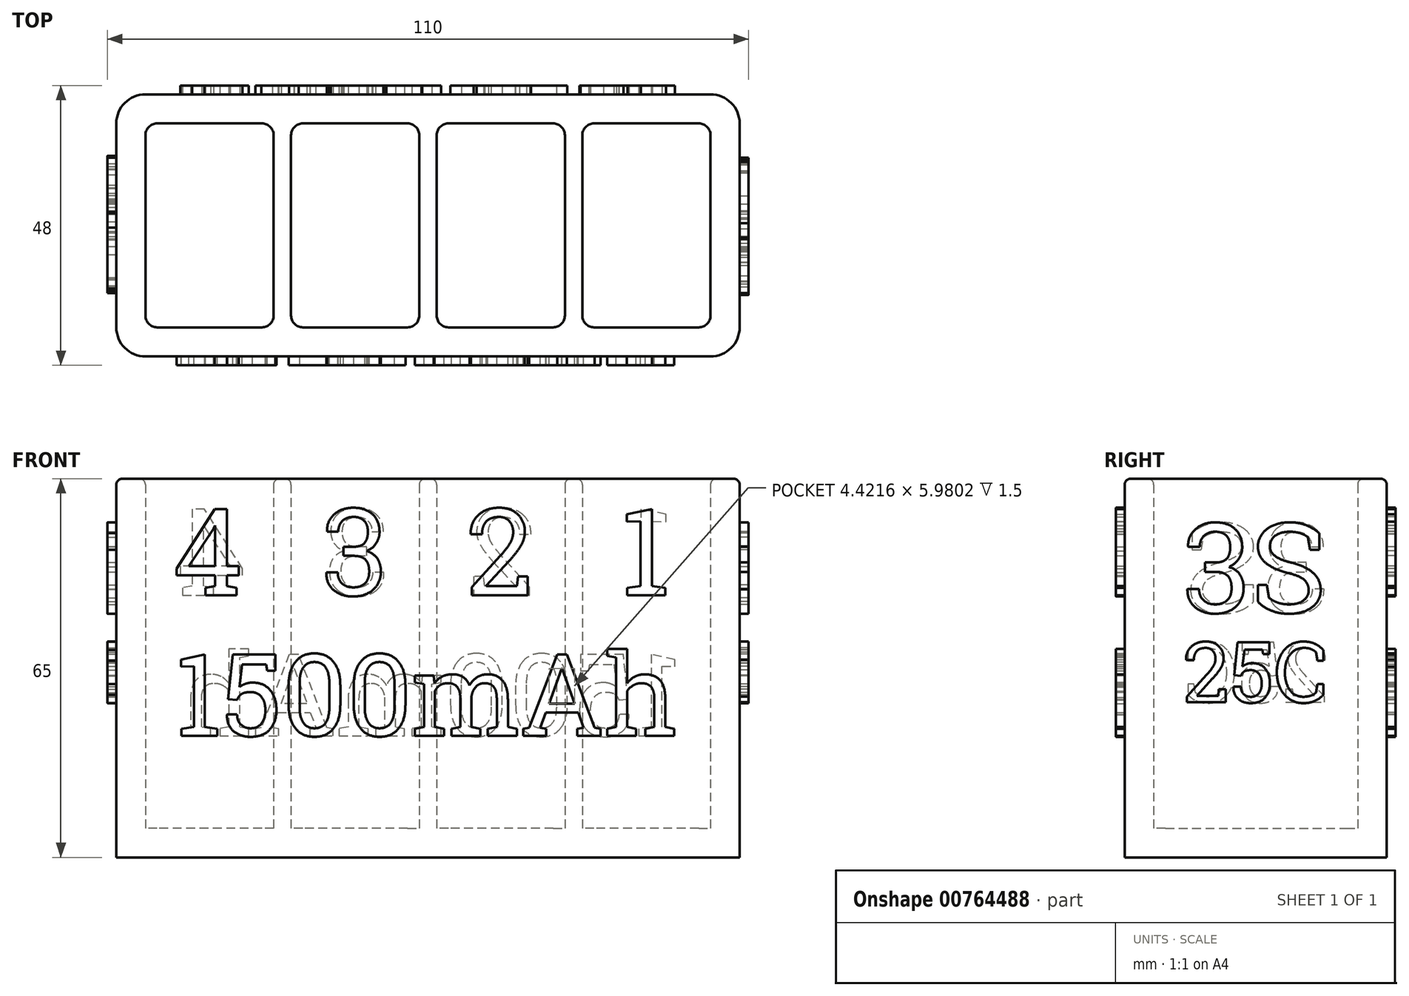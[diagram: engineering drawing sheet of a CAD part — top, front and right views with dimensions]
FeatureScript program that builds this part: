
annotation { "Feature Type Name" : "Feature", "Feature Type Description" : "" }
export const myFeature = defineFeature(function(context is Context, id is Id, definition is map)
    precondition{}
    {
        {
            var Q0;
            Q0=qCreatedBy(makeId("Top.planeOp"),FACE);
            var sketch = newSketch(context, id + "F0", { "sketchPlane" : qUnion([Q0])});
            skLineSegment(sketch, "E0.bottom", {"start": v(53.5, -22.5) * mm, "end": v(-53.5, -22.5) * mm});
            skLineSegment(sketch, "E0.top", {"start": v(53.5, 22.5) * mm, "end": v(-53.5, 22.5) * mm});
            skLineSegment(sketch, "E0.left", {"start": v(53.5, -22.5) * mm, "end": v(53.5, 22.5) * mm});
            skLineSegment(sketch, "E0.right", {"start": v(-53.5, -22.5) * mm, "end": v(-53.5, 22.5) * mm});
            skPoint(sketch, "E0.middle", {"position": v(0, 0) * mm});
            skLineSegment(sketch, "E1.bottom", {"start": v(-26.5, -17.5) * mm, "end": v(-48.5, -17.5) * mm});
            skLineSegment(sketch, "E1.top", {"start": v(-26.5, 17.5) * mm, "end": v(-48.5, 17.5) * mm});
            skLineSegment(sketch, "E1.left", {"start": v(-26.5, -17.5) * mm, "end": v(-26.5, 17.5) * mm});
            skLineSegment(sketch, "E1.right", {"start": v(-48.5, -17.5) * mm, "end": v(-48.5, 17.5) * mm});
            skPoint(sketch, "E1.middle", {"position": v(-37.5, 0) * mm});
            skLineSegment(sketch, "E2.1.0.0", {"start": v(-1.5, 17.5) * mm, "end": v(-23.5, 17.5) * mm});
            skLineSegment(sketch, "E2.1.0.1", {"start": v(-23.5, -17.5) * mm, "end": v(-23.5, 17.5) * mm});
            skLineSegment(sketch, "E2.1.0.2", {"start": v(-1.5, -17.5) * mm, "end": v(-23.5, -17.5) * mm});
            skLineSegment(sketch, "E2.1.0.3", {"start": v(-1.5, -17.5) * mm, "end": v(-1.5, 17.5) * mm});
            skLineSegment(sketch, "E2.2.0.0", {"start": v(23.5, 17.5) * mm, "end": v(1.5, 17.5) * mm});
            skLineSegment(sketch, "E2.2.0.1", {"start": v(1.5, -17.5) * mm, "end": v(1.5, 17.5) * mm});
            skLineSegment(sketch, "E2.2.0.2", {"start": v(23.5, -17.5) * mm, "end": v(1.5, -17.5) * mm});
            skLineSegment(sketch, "E2.2.0.3", {"start": v(23.5, -17.5) * mm, "end": v(23.5, 17.5) * mm});
            skLineSegment(sketch, "E2.3.0.0", {"start": v(48.5, 17.5) * mm, "end": v(26.5, 17.5) * mm});
            skLineSegment(sketch, "E2.3.0.1", {"start": v(26.5, -17.5) * mm, "end": v(26.5, 17.5) * mm});
            skLineSegment(sketch, "E2.3.0.2", {"start": v(48.5, -17.5) * mm, "end": v(26.5, -17.5) * mm});
            skLineSegment(sketch, "E2.3.0.3", {"start": v(48.5, -17.5) * mm, "end": v(48.5, 17.5) * mm});
            skLineSegment(sketch, "E2.direction1", {"start": v(-48.5, 17.5) * mm, "end": v(-23.5, 17.5) * mm, "construction": true});
            skSolve(sketch);
        }
        {
            var Q0;
            Q0=makeQuery(id+"F0.imprint","IMPRINT",FACE,{"disambiguationData":[TD([[makeQuery(id+"F0.imprint","IMPRINT",EDGE,{"derivedFrom":sQuery(id+"F0.wireOp",EDGE,"E0.bottom")}),-1.0]])]});
            var Q1;
            Q1=makeQuery(id+"F0.imprint","IMPRINT",FACE,{"disambiguationData":[TD([[makeQuery(id+"F0.imprint","IMPRINT",EDGE,{"derivedFrom":sQuery(id+"F0.wireOp",EDGE,"E2.2.0.0")}),1.0]])]});
            var Q2;
            Q2=makeQuery(id+"F0.imprint","IMPRINT",FACE,{"disambiguationData":[TD([[makeQuery(id+"F0.imprint","IMPRINT",EDGE,{"derivedFrom":sQuery(id+"F0.wireOp",EDGE,"E2.3.0.0")}),1.0]])]});
            var Q3;
            Q3=makeQuery(id+"F0.imprint","IMPRINT",FACE,{"disambiguationData":[TD([[makeQuery(id+"F0.imprint","IMPRINT",EDGE,{"derivedFrom":sQuery(id+"F0.wireOp",EDGE,"E2.1.0.0")}),1.0]])]});
            var Q4;
            Q4=makeQuery(id+"F0.imprint","IMPRINT",FACE,{"disambiguationData":[TD([[makeQuery(id+"F0.imprint","IMPRINT",EDGE,{"derivedFrom":sQuery(id+"F0.wireOp",EDGE,"E1.bottom")}),-1.0]])]});
            extrude(context, id + "F1", {"entities" : qUnion([Q0, Q1, Q2, Q3, Q4]), "oppositeDirection" : true, "depth" : 5 * mm, "offsetDistance" : 25 * mm});
        }
        {
            var Q0;
            Q0=makeQuery(id+"F0.imprint","IMPRINT",FACE,{"disambiguationData":[TD([[makeQuery(id+"F0.imprint","IMPRINT",EDGE,{"derivedFrom":sQuery(id+"F0.wireOp",EDGE,"E0.bottom")}),-1.0]])]});
            extrude(context, id + "F2", {"entities" : qUnion([Q0]), "operationType" : NewBodyOperationType.ADD, "depth" : 60 * mm, "offsetDistance" : 25 * mm});
        }
        {
            var Q0;
            Q0=makeQuery(id+"F2.opExtrude","SWEPT_EDGE",EDGE,{"disambiguationData":[OSD([sQuery(id+"F0.wireOp",EDGE,"E1.top"),sQuery(id+"F0.wireOp",EDGE,"E1.right")])]});
            var Q1;
            Q1=makeQuery(id+"F2.opExtrude","SWEPT_EDGE",EDGE,{"disambiguationData":[OSD([sQuery(id+"F0.wireOp",EDGE,"E1.bottom"),sQuery(id+"F0.wireOp",EDGE,"E1.right")])]});
            var Q2;
            Q2=makeQuery(id+"F2.opExtrude","SWEPT_EDGE",EDGE,{"disambiguationData":[OSD([sQuery(id+"F0.wireOp",EDGE,"E1.bottom"),sQuery(id+"F0.wireOp",EDGE,"E1.left")])]});
            var Q3;
            Q3=makeQuery(id+"F2.opExtrude","SWEPT_EDGE",EDGE,{"disambiguationData":[OSD([sQuery(id+"F0.wireOp",EDGE,"E1.top"),sQuery(id+"F0.wireOp",EDGE,"E1.left")])]});
            var Q4;
            Q4=makeQuery(id+"F2.opExtrude","SWEPT_EDGE",EDGE,{"disambiguationData":[OSD([sQuery(id+"F0.wireOp",EDGE,"E2.1.0.0"),sQuery(id+"F0.wireOp",EDGE,"E2.1.0.3")])]});
            var Q5;
            Q5=makeQuery(id+"F2.opExtrude","SWEPT_EDGE",EDGE,{"disambiguationData":[OSD([sQuery(id+"F0.wireOp",EDGE,"E2.2.0.0"),sQuery(id+"F0.wireOp",EDGE,"E2.2.0.3")])]});
            var Q6;
            Q6=makeQuery(id+"F2.opExtrude","SWEPT_EDGE",EDGE,{"disambiguationData":[OSD([sQuery(id+"F0.wireOp",EDGE,"E2.3.0.0"),sQuery(id+"F0.wireOp",EDGE,"E2.3.0.3")])]});
            var Q7;
            Q7=makeQuery(id+"F2.opExtrude","SWEPT_EDGE",EDGE,{"disambiguationData":[OSD([sQuery(id+"F0.wireOp",EDGE,"E2.1.0.2"),sQuery(id+"F0.wireOp",EDGE,"E2.1.0.3")])]});
            var Q8;
            Q8=makeQuery(id+"F2.opExtrude","SWEPT_EDGE",EDGE,{"disambiguationData":[OSD([sQuery(id+"F0.wireOp",EDGE,"E2.2.0.2"),sQuery(id+"F0.wireOp",EDGE,"E2.2.0.3")])]});
            var Q9;
            Q9=makeQuery(id+"F2.opExtrude","SWEPT_EDGE",EDGE,{"disambiguationData":[OSD([sQuery(id+"F0.wireOp",EDGE,"E2.3.0.2"),sQuery(id+"F0.wireOp",EDGE,"E2.3.0.3")])]});
            var Q10;
            Q10=makeQuery(id+"F2.opExtrude","SWEPT_EDGE",EDGE,{"disambiguationData":[OSD([sQuery(id+"F0.wireOp",EDGE,"E2.3.0.1"),sQuery(id+"F0.wireOp",EDGE,"E2.3.0.2")])]});
            var Q11;
            Q11=makeQuery(id+"F2.opExtrude","SWEPT_EDGE",EDGE,{"disambiguationData":[OSD([sQuery(id+"F0.wireOp",EDGE,"E2.2.0.1"),sQuery(id+"F0.wireOp",EDGE,"E2.2.0.2")])]});
            var Q12;
            Q12=makeQuery(id+"F2.opExtrude","SWEPT_EDGE",EDGE,{"disambiguationData":[OSD([sQuery(id+"F0.wireOp",EDGE,"E2.1.0.1"),sQuery(id+"F0.wireOp",EDGE,"E2.1.0.2")])]});
            var Q13;
            Q13=makeQuery(id+"F2.opExtrude","SWEPT_EDGE",EDGE,{"disambiguationData":[OSD([sQuery(id+"F0.wireOp",EDGE,"E2.1.0.0"),sQuery(id+"F0.wireOp",EDGE,"E2.1.0.1")])]});
            var Q14;
            Q14=makeQuery(id+"F2.opExtrude","SWEPT_EDGE",EDGE,{"disambiguationData":[OSD([sQuery(id+"F0.wireOp",EDGE,"E2.2.0.0"),sQuery(id+"F0.wireOp",EDGE,"E2.2.0.1")])]});
            var Q15;
            Q15=makeQuery(id+"F2.opExtrude","SWEPT_EDGE",EDGE,{"disambiguationData":[OSD([sQuery(id+"F0.wireOp",EDGE,"E2.3.0.0"),sQuery(id+"F0.wireOp",EDGE,"E2.3.0.1")])]});
            fillet(context, id + "F3", {"entities" : qUnion([Q0, Q1, Q2, Q3, Q4, Q5, Q6, Q7, Q8, Q9, Q10, Q11, Q12, Q13, Q14, Q15]), "radius" : 2 * mm, "tangentPropagation" : true, "allowEdgeOverflow" : false});
        }
        {
            var Q0;
            {var subQ0=sQuery(id+"F0.wireOp",EDGE,"E0.right");var subQ1=sQuery(id+"F0.wireOp",EDGE,"E0.bottom");Q0=makeQuery(id+"F2.boolean.opBoolean","MERGE",EDGE,{"derivedFrom":[makeQuery(id+"F1.opExtrude","SWEPT_EDGE",EDGE,{"disambiguationData":[OSD([subQ1,subQ0])]}),makeQuery(id+"F2.opExtrude","SWEPT_EDGE",EDGE,{"disambiguationData":[OSD([subQ1,subQ0])]})]});}
            var Q1;
            {var subQ0=sQuery(id+"F0.wireOp",EDGE,"E0.left");var subQ1=sQuery(id+"F0.wireOp",EDGE,"E0.bottom");Q1=makeQuery(id+"F2.boolean.opBoolean","MERGE",EDGE,{"derivedFrom":[makeQuery(id+"F1.opExtrude","SWEPT_EDGE",EDGE,{"disambiguationData":[OSD([subQ1,subQ0])]}),makeQuery(id+"F2.opExtrude","SWEPT_EDGE",EDGE,{"disambiguationData":[OSD([subQ1,subQ0])]})]});}
            var Q2;
            {var subQ0=sQuery(id+"F0.wireOp",EDGE,"E0.left");var subQ1=sQuery(id+"F0.wireOp",EDGE,"E0.top");Q2=makeQuery(id+"F2.boolean.opBoolean","MERGE",EDGE,{"derivedFrom":[makeQuery(id+"F1.opExtrude","SWEPT_EDGE",EDGE,{"disambiguationData":[OSD([subQ1,subQ0])]}),makeQuery(id+"F2.opExtrude","SWEPT_EDGE",EDGE,{"disambiguationData":[OSD([subQ1,subQ0])]})]});}
            var Q3;
            {var subQ0=sQuery(id+"F0.wireOp",EDGE,"E0.right");var subQ1=sQuery(id+"F0.wireOp",EDGE,"E0.top");Q3=makeQuery(id+"F2.boolean.opBoolean","MERGE",EDGE,{"derivedFrom":[makeQuery(id+"F1.opExtrude","SWEPT_EDGE",EDGE,{"disambiguationData":[OSD([subQ1,subQ0])]}),makeQuery(id+"F2.opExtrude","SWEPT_EDGE",EDGE,{"disambiguationData":[OSD([subQ1,subQ0])]})]});}
            fillet(context, id + "F4", {"entities" : qUnion([Q0, Q1, Q2, Q3]), "radius" : 5 * mm, "tangentPropagation" : true, "allowEdgeOverflow" : false});
        }
        {
            var Q0;
            Q0=makeQuery(id+"F2.opExtrude","CAP_EDGE",EDGE,{"disambiguationData":[OSD([sQuery(id+"F0.wireOp",EDGE,"E1.top")])],"isStart":false});
            var Q1;
            {var subQ0=sQuery(id+"F0.wireOp",EDGE,"E1.right");var subQ1=sQuery(id+"F0.wireOp",EDGE,"E1.top");Q1=makeQuery(id+"F3.opFillet","BLEND_EDGE",EDGE,{"blendedFrom":[makeQuery(id+"F2.opExtrude","SWEPT_EDGE",EDGE,{"disambiguationData":[OSD([subQ1,subQ0])]}),makeQuery(id+"F2.opExtrude","CAP_FACE",FACE,{"disambiguationData":[OSD([sQuery(id+"F0.wireOp",EDGE,"E0.bottom"),sQuery(id+"F0.wireOp",EDGE,"E0.top"),sQuery(id+"F0.wireOp",EDGE,"E0.left"),sQuery(id+"F0.wireOp",EDGE,"E0.right"),sQuery(id+"F0.wireOp",EDGE,"E1.bottom"),subQ1,sQuery(id+"F0.wireOp",EDGE,"E1.left"),subQ0,sQuery(id+"F0.wireOp",EDGE,"E2.1.0.0"),sQuery(id+"F0.wireOp",EDGE,"E2.1.0.1"),sQuery(id+"F0.wireOp",EDGE,"E2.1.0.2"),sQuery(id+"F0.wireOp",EDGE,"E2.1.0.3"),sQuery(id+"F0.wireOp",EDGE,"E2.2.0.0"),sQuery(id+"F0.wireOp",EDGE,"E2.2.0.1"),sQuery(id+"F0.wireOp",EDGE,"E2.2.0.2"),sQuery(id+"F0.wireOp",EDGE,"E2.2.0.3"),sQuery(id+"F0.wireOp",EDGE,"E2.3.0.0"),sQuery(id+"F0.wireOp",EDGE,"E2.3.0.1"),sQuery(id+"F0.wireOp",EDGE,"E2.3.0.2"),sQuery(id+"F0.wireOp",EDGE,"E2.3.0.3")])],"isStart":false})],"blendedInto":[makeQuery(id+"F2.opExtrude","CAP_FACE",FACE,{"disambiguationData":[OSD([sQuery(id+"F0.wireOp",EDGE,"E0.bottom"),sQuery(id+"F0.wireOp",EDGE,"E0.top"),sQuery(id+"F0.wireOp",EDGE,"E0.left"),sQuery(id+"F0.wireOp",EDGE,"E0.right"),sQuery(id+"F0.wireOp",EDGE,"E1.bottom"),subQ1,sQuery(id+"F0.wireOp",EDGE,"E1.left"),subQ0,sQuery(id+"F0.wireOp",EDGE,"E2.1.0.0"),sQuery(id+"F0.wireOp",EDGE,"E2.1.0.1"),sQuery(id+"F0.wireOp",EDGE,"E2.1.0.2"),sQuery(id+"F0.wireOp",EDGE,"E2.1.0.3"),sQuery(id+"F0.wireOp",EDGE,"E2.2.0.0"),sQuery(id+"F0.wireOp",EDGE,"E2.2.0.1"),sQuery(id+"F0.wireOp",EDGE,"E2.2.0.2"),sQuery(id+"F0.wireOp",EDGE,"E2.2.0.3"),sQuery(id+"F0.wireOp",EDGE,"E2.3.0.0"),sQuery(id+"F0.wireOp",EDGE,"E2.3.0.1"),sQuery(id+"F0.wireOp",EDGE,"E2.3.0.2"),sQuery(id+"F0.wireOp",EDGE,"E2.3.0.3")])],"isStart":false})]});}
            var Q2;
            {var subQ0=sQuery(id+"F0.wireOp",EDGE,"E1.right");Q2=makeQuery(id+"F3.opFillet","BLEND_EDGE",EDGE,{"blendedFrom":[makeQuery(id+"F2.opExtrude","SWEPT_EDGE",EDGE,{"disambiguationData":[OSD([sQuery(id+"F0.wireOp",EDGE,"E1.top"),subQ0])]}),makeQuery(id+"F2.opExtrude","SWEPT_FACE",FACE,{"disambiguationData":[OSD([subQ0])]})],"blendedInto":[makeQuery(id+"F2.opExtrude","SWEPT_FACE",FACE,{"disambiguationData":[OSD([subQ0])]})]});}
            var Q3;
            Q3=makeQuery(id+"F2.opExtrude","CAP_EDGE",EDGE,{"disambiguationData":[OSD([sQuery(id+"F0.wireOp",EDGE,"E2.1.0.0")])],"isStart":false});
            var Q4;
            Q4=makeQuery(id+"F2.opExtrude","CAP_EDGE",EDGE,{"disambiguationData":[OSD([sQuery(id+"F0.wireOp",EDGE,"E2.2.0.0")])],"isStart":false});
            var Q5;
            Q5=makeQuery(id+"F2.opExtrude","CAP_EDGE",EDGE,{"disambiguationData":[OSD([sQuery(id+"F0.wireOp",EDGE,"E2.3.0.0")])],"isStart":false});
            fillet(context, id + "F5", {"entities" : qUnion([Q0, Q1, Q2, Q3, Q4, Q5]), "radius" : 1 * mm, "tangentPropagation" : true, "allowEdgeOverflow" : false});
        }
        {
            var Q0;
            Q0=makeQuery(id+"F2.opExtrude","CAP_FACE",FACE,{"disambiguationData":[OSD([sQuery(id+"F0.wireOp",EDGE,"E0.bottom"),sQuery(id+"F0.wireOp",EDGE,"E0.top"),sQuery(id+"F0.wireOp",EDGE,"E0.left"),sQuery(id+"F0.wireOp",EDGE,"E0.right"),sQuery(id+"F0.wireOp",EDGE,"E1.bottom"),sQuery(id+"F0.wireOp",EDGE,"E1.top"),sQuery(id+"F0.wireOp",EDGE,"E1.left"),sQuery(id+"F0.wireOp",EDGE,"E1.right"),sQuery(id+"F0.wireOp",EDGE,"E2.1.0.0"),sQuery(id+"F0.wireOp",EDGE,"E2.1.0.1"),sQuery(id+"F0.wireOp",EDGE,"E2.1.0.2"),sQuery(id+"F0.wireOp",EDGE,"E2.1.0.3"),sQuery(id+"F0.wireOp",EDGE,"E2.2.0.0"),sQuery(id+"F0.wireOp",EDGE,"E2.2.0.1"),sQuery(id+"F0.wireOp",EDGE,"E2.2.0.2"),sQuery(id+"F0.wireOp",EDGE,"E2.2.0.3"),sQuery(id+"F0.wireOp",EDGE,"E2.3.0.0"),sQuery(id+"F0.wireOp",EDGE,"E2.3.0.1"),sQuery(id+"F0.wireOp",EDGE,"E2.3.0.2"),sQuery(id+"F0.wireOp",EDGE,"E2.3.0.3")])],"isStart":false});
            var sketch = newSketch(context, id + "F6", { "sketchPlane" : qUnion([Q0])});
            skPoint(sketch, "E3", {"position": v(37.5, 22.5) * mm});
            skPoint(sketch, "E3.positionSnap0", {"position": v(37.5, 18.5) * mm});
            skPoint(sketch, "E4", {"position": v(12.5, 22.5) * mm});
            skPoint(sketch, "E4.positionSnap0", {"position": v(12.5, 18.5) * mm});
            skPoint(sketch, "E5", {"position": v(-12.5, 22.5) * mm});
            skPoint(sketch, "E5.positionSnap0", {"position": v(-12.5, 18.5) * mm});
            skPoint(sketch, "E6", {"position": v(-37.5, 22.5) * mm});
            skPoint(sketch, "E6.positionSnap0", {"position": v(-37.5, 18.5) * mm});
            skPoint(sketch, "E7", {"position": v(-37.5, -22.5) * mm});
            skPoint(sketch, "E7.positionSnap0", {"position": v(-37.5, -18.5) * mm});
            skPoint(sketch, "E8", {"position": v(-12.5, -22.5) * mm});
            skPoint(sketch, "E9", {"position": v(-12.5, -18.5) * mm});
            skPoint(sketch, "E10", {"position": v(12.5, -18.5) * mm});
            skPoint(sketch, "E11", {"position": v(12.5, -22.5) * mm});
            skPoint(sketch, "E12", {"position": v(37.5, -18.5) * mm});
            skPoint(sketch, "E13", {"position": v(37.5, -22.5) * mm});
            skSolve(sketch);
        }
        {
            var Q0;
            {var subQ0=sQuery(id+"F0.wireOp",EDGE,"E0.top");Q0=makeQuery(id+"F2.boolean.opBoolean","MERGE",FACE,{"derivedFrom":[makeQuery(id+"F1.opExtrude","SWEPT_FACE",FACE,{"disambiguationData":[OSD([subQ0])]}),makeQuery(id+"F2.opExtrude","SWEPT_FACE",FACE,{"disambiguationData":[OSD([subQ0])]})]});}
            var sketch = newSketch(context, id + "F7", { "sketchPlane" : qUnion([Q0])});
            skText(sketch, "E14", { "text": "1", "fontName": "RobotoSlab-Regular.ttf"});
            skText(sketch, "E15", { "text": "2", "fontName": "RobotoSlab-Regular.ttf"});
            skText(sketch, "E16", { "text": "3", "fontName": "RobotoSlab-Regular.ttf"});
            skText(sketch, "E17", { "text": "4", "fontName": "RobotoSlab-Regular.ttf"});
            skLineSegment(sketch, "E18", {"start": v(-54.85, 55) * mm, "end": v(56.37, 55) * mm, "construction": true});
            skLineSegment(sketch, "E19", {"start": v(-37.5, 60) * mm, "end": v(-37.5, 29.3) * mm, "construction": true});
            skLineSegment(sketch, "E20", {"start": v(-12.5, 60) * mm, "end": v(-12.5, 29.73) * mm, "construction": true});
            skLineSegment(sketch, "E21", {"start": v(12.5, 60) * mm, "end": v(12.5, 29) * mm, "construction": true});
            skLineSegment(sketch, "E22", {"start": v(37.5, 60) * mm, "end": v(37.5, 28.2) * mm, "construction": true});
            skLineSegment(sketch, "E23", {"start": v(-56.25, 40) * mm, "end": v(59.34, 40) * mm, "construction": true});
            skText(sketch, "E24", { "text": "1500mAh", "fontName": "RobotoSlab-Regular.ttf"});
            const initialGuessF7  = {"E14": [-0.04205, 0.04, 1, 0, 0.015], "E15": [-0.01844, 0.04, 1, 0, 0.015], "E16": [0.0068, 0.04, 1, 0, 0.015], "E17": [0.03119, 0.04, 1, 0, 0.015], "E24": [-0.0435, 0.01589, 1, 0, 0.01411]};
            skSetInitialGuess(sketch, initialGuessF7);
            skSolve(sketch);
        }
        {
            var Q0;
            {var subQ0=sQuery(id+"F0.wireOp",EDGE,"E0.bottom");Q0=makeQuery(id+"F2.boolean.opBoolean","MERGE",FACE,{"derivedFrom":[makeQuery(id+"F1.opExtrude","SWEPT_FACE",FACE,{"disambiguationData":[OSD([subQ0])]}),makeQuery(id+"F2.opExtrude","SWEPT_FACE",FACE,{"disambiguationData":[OSD([subQ0])]})]});}
            var sketch = newSketch(context, id + "F8", { "sketchPlane" : qUnion([Q0])});
            skLineSegment(sketch, "E25", {"start": v(-59.89, 55) * mm, "end": v(65.59, 55) * mm, "construction": true});
            skLineSegment(sketch, "E26", {"start": v(-59.89, 40) * mm, "end": v(64.96, 40) * mm, "construction": true});
            skText(sketch, "E27", { "text": "1", "fontName": "RobotoSlab-Regular.ttf"});
            skText(sketch, "E28", { "text": "2", "fontName": "RobotoSlab-Regular.ttf"});
            skText(sketch, "E29", { "text": "3", "fontName": "RobotoSlab-Regular.ttf"});
            skText(sketch, "E30", { "text": "4", "fontName": "RobotoSlab-Regular.ttf"});
            skText(sketch, "E31", { "text": "1500mAh", "fontName": "RobotoSlab-Regular.ttf"});
            const initialGuessF8  = {"E27": [0.03295, 0.04, 1, 0, 0.015], "E28": [0.00656, 0.04, 1, 0, 0.015], "E29": [-0.0182, 0.04, 1, 0, 0.015], "E30": [-0.04381, 0.04, 1, 0, 0.015], "E31": [-0.0435, 0.01589, 1, 0, 0.01411]};
            skSetInitialGuess(sketch, initialGuessF8);
            skSolve(sketch);
        }
        {
            var Q0;
            Q0 = qSketchRegion(id + "F7", true);
            extrude(context, id + "F9", {"entities" : qUnion([Q0]), "operationType" : NewBodyOperationType.ADD, "depth" : 1.5 * mm, "offsetDistance" : 25 * mm});
        }
        {
            var Q0;
            Q0 = qSketchRegion(id + "F8", true);
            extrude(context, id + "F10", {"entities" : qUnion([Q0]), "operationType" : NewBodyOperationType.ADD, "depth" : 1.5 * mm, "offsetDistance" : 25 * mm});
        }
        {
            var Q0;
            {var subQ0=sQuery(id+"F0.wireOp",EDGE,"E0.left");Q0=makeQuery(id+"F2.boolean.opBoolean","MERGE",FACE,{"derivedFrom":[makeQuery(id+"F1.opExtrude","SWEPT_FACE",FACE,{"disambiguationData":[OSD([subQ0])]}),makeQuery(id+"F2.opExtrude","SWEPT_FACE",FACE,{"disambiguationData":[OSD([subQ0])]})]});}
            var sketch = newSketch(context, id + "F11", { "sketchPlane" : qUnion([Q0])});
            skText(sketch, "E32", { "text": "3S", "fontName": "RobotoSlab-Regular.ttf"});
            skText(sketch, "E33", { "text": "25C", "fontName": "RobotoSlab-Regular.ttf"});
            const initialGuessF11  = {"E32": [-0.0125, 0.03704, 1, 0, 0.01546], "E33": [-0.0125, 0.02162, 1, 0, 0.01042]};
            skSetInitialGuess(sketch, initialGuessF11);
            skSolve(sketch);
        }
        {
            var Q0;
            Q0 = qSketchRegion(id + "F11", true);
            extrude(context, id + "F12", {"entities" : qUnion([Q0]), "operationType" : NewBodyOperationType.ADD, "depth" : 1.5 * mm, "offsetDistance" : 25 * mm});
        }
        {
            var Q0;
            {var subQ0=sQuery(id+"F0.wireOp",EDGE,"E0.right");Q0=makeQuery(id+"F2.boolean.opBoolean","MERGE",FACE,{"derivedFrom":[makeQuery(id+"F1.opExtrude","SWEPT_FACE",FACE,{"disambiguationData":[OSD([subQ0])]}),makeQuery(id+"F2.opExtrude","SWEPT_FACE",FACE,{"disambiguationData":[OSD([subQ0])]})]});}
            var sketch = newSketch(context, id + "F13", { "sketchPlane" : qUnion([Q0])});
            skText(sketch, "E34", { "text": "3S", "fontName": "RobotoSlab-Regular.ttf"});
            skText(sketch, "E35", { "text": "25C", "fontName": "RobotoSlab-Regular.ttf"});
            const initialGuessF13  = {"E34": [-0.0125, 0.03704, 1, 0, 0.01546], "E35": [-0.0125, 0.02162, 1, 0, 0.01042]};
            skSetInitialGuess(sketch, initialGuessF13);
            skSolve(sketch);
        }
        {
            var Q0;
            Q0 = qSketchRegion(id + "F13", true);
            extrude(context, id + "F14", {"entities" : qUnion([Q0]), "operationType" : NewBodyOperationType.ADD, "depth" : 1.5 * mm, "offsetDistance" : 25 * mm});
        }
        {
            var Q0;
            Q0=makeQuery(id+"F2.opExtrude","CAP_EDGE",EDGE,{"disambiguationData":[OSD([sQuery(id+"F0.wireOp",EDGE,"E0.bottom")])],"isStart":false});
            fillet(context, id + "F15", {"entities" : qUnion([Q0]), "radius" : 1 * mm, "tangentPropagation" : true, "allowEdgeOverflow" : false});
        }
    });
